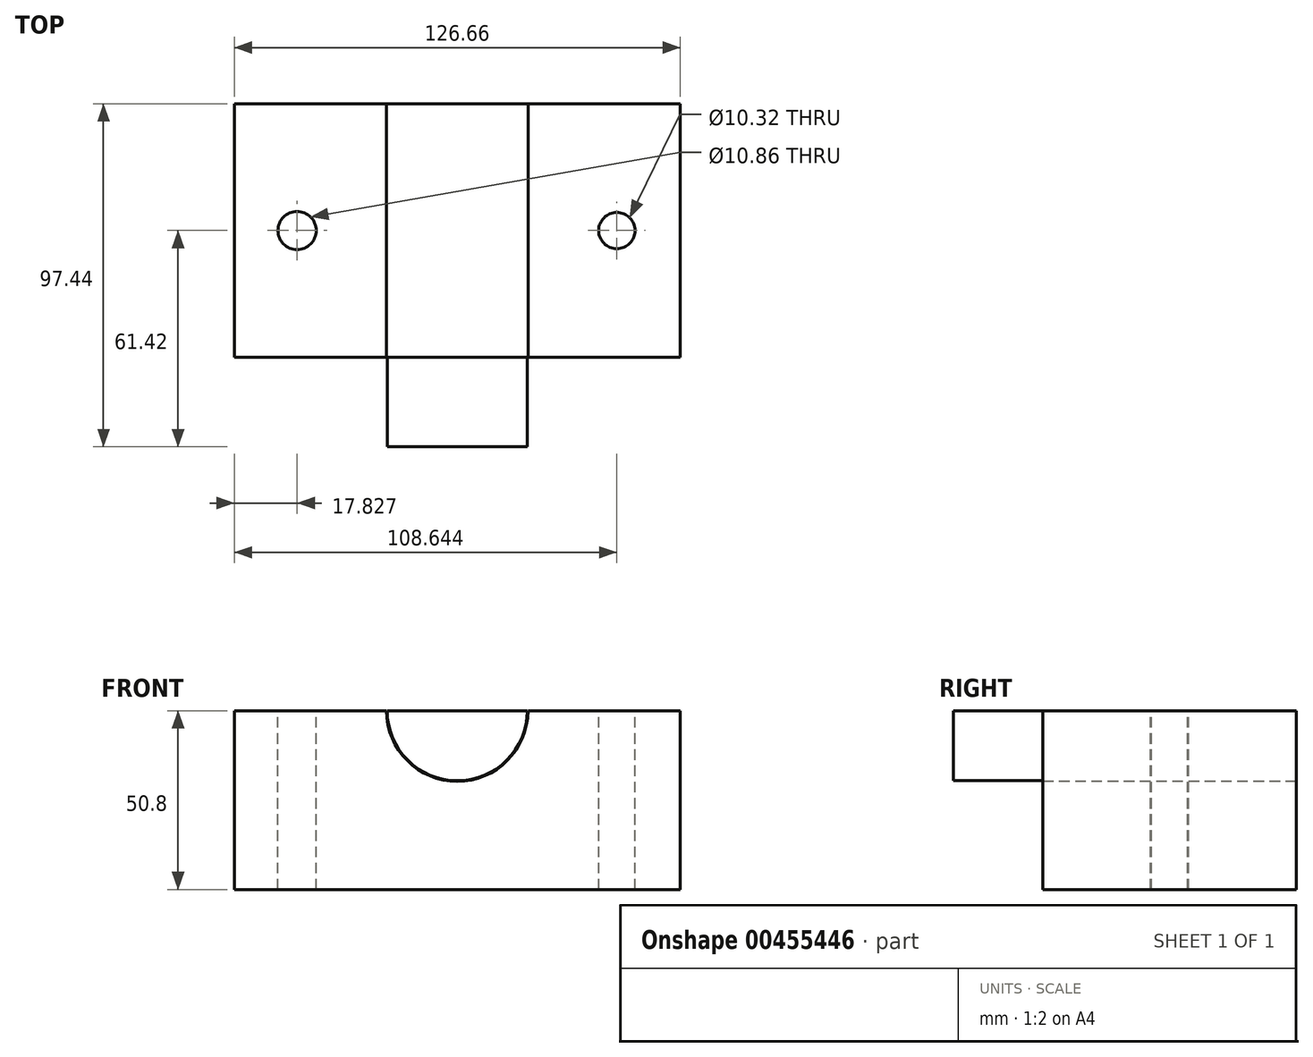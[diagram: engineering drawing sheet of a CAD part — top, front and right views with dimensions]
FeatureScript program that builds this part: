
annotation { "Feature Type Name" : "Feature", "Feature Type Description" : "" }
export const myFeature = defineFeature(function(context is Context, id is Id, definition is map)
    precondition{}
    {
        {
            var Q0;
            Q0=qCreatedBy(makeId("Top.planeOp"),FACE);
            var sketch = newSketch(context, id + "F0", { "sketchPlane" : qUnion([Q0])});
            skLineSegment(sketch, "E0.bottom", {"start": v(63.33, -36.02) * mm, "end": v(-63.33, -36.02) * mm});
            skLineSegment(sketch, "E0.top", {"start": v(63.33, 36.02) * mm, "end": v(-63.33, 36.02) * mm});
            skLineSegment(sketch, "E0.left", {"start": v(63.33, -36.02) * mm, "end": v(63.33, 36.02) * mm});
            skLineSegment(sketch, "E0.right", {"start": v(-63.33, -36.02) * mm, "end": v(-63.33, 36.02) * mm});
            skPoint(sketch, "E0.middle", {"position": v(0, 0) * mm});
            skSolve(sketch);
        }
        {
            var Q0;
            Q0 = qSketchRegion(id + "F0", true);
            extrude(context, id + "F1", {"entities" : qUnion([Q0]), "depth" : 50.8 * mm});
        }
        {
            var Q0;
            Q0=makeQuery(id+"F1.opExtrude","SWEPT_FACE",FACE,{"disambiguationData":[OSD([sQuery(id+"F0.wireOp",EDGE,"E0.bottom")])]});
            var sketch = newSketch(context, id + "F2", { "sketchPlane" : qUnion([Q0])});
            skArc(sketch, "E1", {"start": v(19.9, 50.8) * mm, "mid": v(0, 30.9) * mm, "end": v(-19.9, 50.8) * mm});
            skArc(sketch, "E2", {"start": v(27.3, 50.8) * mm, "mid": v(0, 23.5) * mm, "end": v(-27.3, 50.8) * mm});
            skSolve(sketch);
        }
        {
            var Q0;
            Q0 = qSketchRegion(id + "F2", true);
            var Q1;
            {var subQ0=sQuery(id+"F2.wireOp",EDGE,"E1");Q1=makeQuery(id+"F2.imprint","IMPRINT",FACE,{"disambiguationData":[TD([[makeQuery(id+"F2.imprint","IMPRINT",EDGE,{"derivedFrom":subQ0}),1.0]])]});}
            extrude(context, id + "F3", {"entities" : qUnion([Q0, Q1]), "operationType" : NewBodyOperationType.ADD, "depth" : 25.4 * mm, "hasSecondDirection" : true, "secondDirectionOppositeDirection" : true, "secondDirectionDepth" : 95.25 * mm});
        }
        {
            var Q0;
            {var subQ0=sQuery(id+"F0.wireOp",EDGE,"E0.bottom");var subQ1=sQuery(id+"F2.wireOp",EDGE,"E1");Q0=makeQuery(id+"F3.boolean.opBoolean","SPLIT",FACE,{"disambiguationData":[TD([makeQuery(id+"F3.opExtrude","SWEPT_FACE",FACE,{"disambiguationData":[OSD([subQ1])]})])],"derivedFrom":makeQuery(id+"F1.opExtrude","SWEPT_FACE",FACE,{"disambiguationData":[OSD([subQ0])]})});}
            var sketch = newSketch(context, id + "F4", { "sketchPlane" : qUnion([Q0])});
            skCircle(sketch, "E3", {"center": v(0, 50.8) * mm, "radius": 20.09 * mm});
            skSolve(sketch);
        }
        {
            var Q0;
            Q0 = qSketchRegion(id + "F4", true);
            extrude(context, id + "F5", {"entities" : qUnion([Q0]), "operationType" : NewBodyOperationType.REMOVE, "endBound" : BoundingType.THROUGH_ALL, "oppositeDirection" : true, "depth" : 25.4 * mm});
        }
        {
            var Q0;
            {var subQ0=sQuery(id+"F0.wireOp",EDGE,"E0.left");var subQ2=sQuery(id+"F2.wireOp",EDGE,"E1");var subQ3=sQuery(id+"F0.wireOp",EDGE,"E0.top");var subQ4=sQuery(id+"F0.wireOp",EDGE,"E0.bottom");var subQ6=makeQuery(id+"F1.opExtrude","CAP_EDGE",EDGE,{"disambiguationData":[OSD([subQ4])],"isStart":false});Q0=makeQuery(id+"F5.boolean.opBoolean","SPLIT",FACE,{"disambiguationData":[TD([makeQuery(id+"F1.opExtrude","SWEPT_FACE",FACE,{"disambiguationData":[OSD([subQ0])]})])],"derivedFrom":makeQuery(id+"F3.boolean.opBoolean","MERGE",FACE,{"derivedFrom":[makeQuery(id+"F1.opExtrude","CAP_FACE",FACE,{"disambiguationData":[OSD([subQ4,subQ3,subQ0,sQuery(id+"F0.wireOp",EDGE,"E0.right")])],"isStart":false}),makeQuery(id+"F3.opExtrude","SWEPT_FACE",FACE,{"disambiguationData":[OSD([subQ4]),TDD([makeQuery(id+"F2.imprint","IMPRINT",EDGE,{"disambiguationData":[TD([[makeQuery(id+"F2.imprint","INTERSECT",VERTEX,{"disambiguationData":[OD(0.0)],"derivedFrom":[subQ6,subQ2]}),1.0]])],"derivedFrom":subQ6})])]}),makeQuery(id+"F3.opExtrude","SWEPT_FACE",FACE,{"disambiguationData":[OSD([subQ4]),TDD([makeQuery(id+"F2.imprint","IMPRINT",EDGE,{"disambiguationData":[TD([[makeQuery(id+"F2.imprint","INTERSECT",VERTEX,{"disambiguationData":[OD(1.0)],"derivedFrom":[subQ6,subQ2]}),-1.0]])],"derivedFrom":subQ6})])]})]})});}
            var sketch = newSketch(context, id + "F6", { "sketchPlane" : qUnion([Q0])});
            skCircle(sketch, "E4", {"center": v(-45.5, 0) * mm, "radius": 5.43 * mm});
            skCircle(sketch, "E5", {"center": v(45.31, 0) * mm, "radius": 5.16 * mm});
            skSolve(sketch);
        }
        {
            var Q0;
            Q0 = qSketchRegion(id + "F6", true);
            extrude(context, id + "F7", {"entities" : qUnion([Q0]), "operationType" : NewBodyOperationType.REMOVE, "endBound" : BoundingType.THROUGH_ALL, "oppositeDirection" : true, "depth" : 25.4 * mm});
        }
    });
